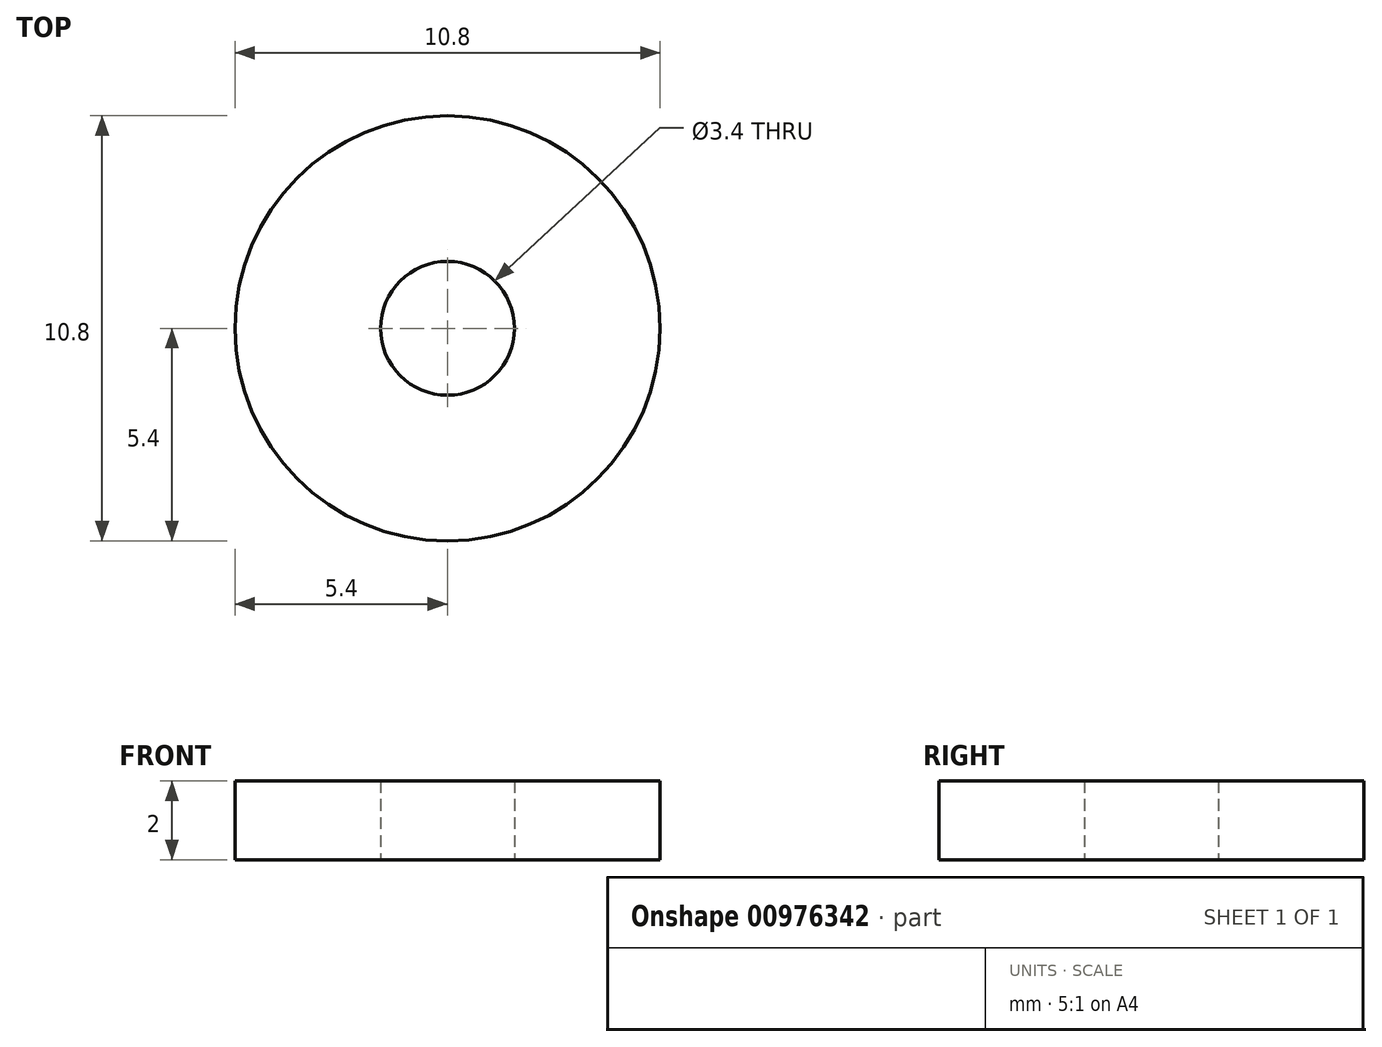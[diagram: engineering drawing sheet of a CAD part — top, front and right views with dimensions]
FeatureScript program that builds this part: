
annotation { "Feature Type Name" : "Feature", "Feature Type Description" : "" }
export const myFeature = defineFeature(function(context is Context, id is Id, definition is map)
    precondition{}
    {
        {
            var Q0;
            Q0=qCreatedBy(makeId("Top.planeOp"),FACE);
            var sketch = newSketch(context, id + "F0", { "sketchPlane" : qUnion([Q0])});
            skCircle(sketch, "E0", {"center": v(0, 0) * mm, "radius": 7.5 * mm});
            skCircle(sketch, "E1", {"center": v(0, 0) * mm, "radius": 1.7 * mm});
            skSolve(sketch);
        }
        {
            var Q0;
            Q0=makeQuery(id+"F0.imprint","IMPRINT",FACE,{"disambiguationData":[TD([[makeQuery(id+"F0.imprint","IMPRINT",EDGE,{"derivedFrom":sQuery(id+"F0.wireOp",EDGE,"E0")}),1.0]])]});
            extrude(context, id + "F1", {"entities" : qUnion([Q0]), "depth" : 2 * mm, "offsetDistance" : 25 * mm});
        }
        {
            var Q0;
            Q0=makeQuery(id+"F1.opExtrude","CAP_FACE",FACE,{"disambiguationData":[OSD([sQuery(id+"F0.wireOp",EDGE,"E0"),sQuery(id+"F0.wireOp",EDGE,"E1")])],"isStart":true});
            var sketch = newSketch(context, id + "F2", { "sketchPlane" : qUnion([Q0])});
            skCircle(sketch, "E2", {"center": v(0, 0) * mm, "radius": 6.5 * mm});
            skCircle(sketch, "E3", {"center": v(0, 0) * mm, "radius": 5.4 * mm});
            skSolve(sketch);
        }
        {
            var Q0;
            Q0=makeQuery(id+"F2.imprint","IMPRINT",FACE,{"disambiguationData":[TD([[makeQuery(id+"F2.imprint","IMPRINT",EDGE,{"derivedFrom":sQuery(id+"F2.wireOp",EDGE,"E2")}),1.0]])]});
            var Q1;
            Q1=makeQuery(id+"F2.imprint","IMPRINT",FACE,{"disambiguationData":[TD([[makeQuery(id+"F2.imprint","IMPRINT",EDGE,{"derivedFrom":sQuery(id+"F2.wireOp",EDGE,"E2")}),-1.0]])]});
            extrude(context, id + "F3", {"entities" : qUnion([Q0, Q1]), "operationType" : NewBodyOperationType.REMOVE, "endBound" : BoundingType.UP_TO_NEXT, "oppositeDirection" : true, "depth" : 25 * mm, "offsetDistance" : 25 * mm});
        }
    });
